# Revit family: Building-ConnessioniIEC309-GEWISS-44IB-PRESE-INTERBLOCCATE_IP44_SENZA_FONDO_FUS
name_source: partatom
category: Apparecchi elettrici
units: mm (PartAtom-declared; Revit-internal decimal feet)

## family parameters
Condiviso = No
Host = Superficie
Mantenere orientamento annotazione = Sì
Punto di calcolo locali = Sì
Quota connettore circolare = Usa diametro
Taglio con vuoti quando caricato = No
Tipo di parte = Normale

## types (22) — shared parameters
BLOCCO = B=C
Catalogo = BUILDING
Catalogo Serie = 44 IB
Codice Electrocod = 2220
Con fondo = No
FORMULA = 1000 mm  [stored 3.28084 ft]
Frequenza = 50/60 Hz
Frequenza nominale (Hz) = 50/60 Hz
Glow Wire Test = 850 °C (Parti attive) - 650 °C (Parti passive)
Glow wire test: = 850 °C (Parti attive) - 650 °C (Parti passive)
Grado di protezione = IP44
IDF = 20820749-807f-45a7-b37a-7863cab2ae49
IDT = d594ee1e-5beb-4100-9b20-8b248744bc80
Immagine tipo = IP44Fus.jpg
L = 155 mm  [stored 0.50853 ft]
N.poli = 1
POMELLO = bianco
PRESA = Giallo
Potere di interruzione fusibili = > 50 kA
Produttore = GEWISS S.p.A.
Prospetto di default = 1219 mm
Protezione = Base portafusibile (CBF)
Resistenza agli urti = IK08
SEO = Presa
STRUTTURA = RAL - 7035
STRUTTURA ALTA = blue
Scheda Tecnica = https://www.gewiss.com
Spostamento_S = 1000 mm  [stored 3.28084 ft]
Temperatura di funzionamento = -25 ÷ +40 °C
Temperatura di utilizzo = -25 +40 °C
Termopressione con biglia = 125 °C
Tipologia = Orizzontale
URL = https://www.gewiss.com
VETRO = Vetro
Versione file RFA = 21.4
Voltaggio = 0 V
W = 115 mm  [stored 0.377297 ft]

## per-type parameters (varying)
| type | Base portafusibile | Codice EAN | Colore | Colore: | Corrente nominale (A) | Corrente nominale (In) | Descrizione | Modello | N. poli | Numero di poli | Riferimento h | Tensione nominale |
| GW66130 - PRESA BL.OR.S.F.3P+T 16A 400V 6H CBF | E14 | 8011564029361 | Rosso | Rosso | 16 | 16 | PRESA BL.OR.S.F.3P+T 16A 400V 6H CBF | GW66130 | 3P+T | 3P+T | 6 | 380-415V |
| GW66131 - PRESA BL.OR.S.F.3P+N+T 16A 400V 6H CBF | E14 | 8011564029378 | Rosso | Rosso | 16 | 16 | PRESA BL.OR.S.F.3P+N+T 16A 400V 6H CBF | GW66131 | 3P+N+T | 3P+N+T | 6 | 380-415V |
| GW66137 - PRESA BL.OR.S.F.2P+T 32A 230V 6H CBF | E18 | 8011564029439 | Blu | Blu | 32 | 32 | PRESA BL.OR.S.F.2P+T 32A 230V 6H CBF | GW66137 | 2P+T | 2P+T | 6 | 200-250V |
| GW66125 - PRESA BL.OR.S.F.3P+N+T 16A 110V 4H CBF | E14 | 8011564029316 | Giallo | Giallo | 16 | 16 | PRESA BL.OR.S.F.3P+N+T 16A 110V 4H CBF | GW66125 | 3P+N+T | 3P+N+T | 4 | 100-130V |
| GW66136 - PRESA BL.OR.S.F.3P+N+T 32A 110V 4H CBF | E18 | 8011564029422 | Giallo | Giallo | 32 | 32 | PRESA BL.OR.S.F.3P+N+T 32A 110V 4H CBF | GW66136 | 3P+N+T | 3P+N+T | 4 | 100-130V |
| GW66132 - PRESA BL.OR.S.F.3P+T 16A 500V 7H CBF | gG | 8011564029385 | Nero | Nero | 16 | 16 | PRESA BL.OR.S.F.3P+T 16A 500V 7H CBF | GW66132 | 3P+T | 3P+T | 7 | 480-500V |
| GW66124 - PRESA BL.OR.S.F.3P+T 16A 110V 4H CBF | E14 | 8011564029309 | Giallo | Giallo | 16 | 16 | PRESA BL.OR.S.F.3P+T 16A 110V 4H CBF | GW66124 | 3P+T | 3P+T | 4 | 100-130V |
| GW66138 - PRESA BL.OR.S.F.3P+T 32A 230V 9H CBF | E18 | 8011564029446 | Blu | Blu | 32 | 32 | PRESA BL.OR.S.F.3P+T 32A 230V 9H CBF | GW66138 | 3P+T | 3P+T | 9 | 200-250V |
| GW66129 - PRESA BL.OR.S.F.2P+T 16A 400V 9H CBF | E14 | 8011564029354 | Rosso | Rosso | 16 | 16 | PRESA BL.OR.S.F.2P+T 16A 400V 9H CBF | GW66129 | 2P+T | 2P+T | 9 | 380-415V |
| GW66140 - PRESA BL.OR.S.F.2P+T 32A 400V 9H CBF | E18 | 8011564029460 | Rosso | Rosso | 32 | 32 | PRESA BL.OR.S.F.2P+T 32A 400V 9H CBF | GW66140 | 2P+T | 2P+T | 9 | 380-415V |
| GW66141 - PRESA BL.OR.S.F.3P+T 32A 400V 6H CBF | E18 | 8011564029477 | Rosso | Rosso | 32 | 32 | PRESA BL.OR.S.F.3P+T 32A 400V 6H CBF | GW66141 | 3P+T | 3P+T | 6 | 380-415V |
| GW66142 - PRESA BL.OR.S.F.3P+N+T 32A 400V 6H CBF | E18 | 8011564029484 | Rosso | Rosso | 32 | 32 | PRESA BL.OR.S.F.3P+N+T 32A 400V 6H CBF | GW66142 | 3P+N+T | 3P+N+T | 6 | 380-415V |
| GW66133 - PRESA BL.OR.S.F.3P+N+T 16A 500V 7H CBF | gG | 8011564029392 | Nero | Nero | 16 | 16 | PRESA BL.OR.S.F.3P+N+T 16A 500V 7H CBF | GW66133 | 3P+N+T | 3P+N+T | 7 | 480-500V |
| GW66134 - PRESA BL.OR.S.F.2P+T 32A 110V 4H CBF | E18 | 8011564029408 | Giallo | Giallo | 32 | 32 | PRESA BL.OR.S.F.2P+T 32A 110V 4H CBF | GW66134 | 2P+T | 2P+T | 4 | 100-130V |
| GW66135 - PRESA BL.OR.S.F.3P+T 32A 110V 4H CBF | E18 | 8011564029415 | Giallo | Giallo | 32 | 32 | PRESA BL.OR.S.F.3P+T 32A 110V 4H CBF | GW66135 | 3P+T | 3P+T | 4 | 100-130V |
| GW66128 - PRESA BL.OR.S.F.3P+N+T 16A 230V 9H CBF | E14 | 8011564029347 | Blu | Blu | 16 | 16 | PRESA BL.OR.S.F.3P+N+T 16A 230V 9H CBF | GW66128 | 3P+N+T | 3P+N+T | 9 | 200-250V |
| GW66143 - PRESA BL.OR.S.F.3P+T 32A 500V 7H CBF | gG | 8011564029491 | Nero | Nero | 32 | 32 | PRESA BL.OR.S.F.3P+T 32A 500V 7H CBF | GW66143 | 3P+T | 3P+T | 7 | 480-500V |
| GW66123 - PRESA BL.OR.S.F.2P+T 16A 110V 4H CBF | E14 | 8011564029293 | Giallo | Giallo | 16 | 16 | PRESA BL.OR.S.F.2P+T 16A 110V 4H CBF | GW66123 | 2P+T | 2P+T | 4 | 100-130V |
| GW66127 - PRESA BL.OR.S.F.3P+T 16A 230V 9H CBF | E14 | 8011564029330 | Blu | Blu | 16 | 16 | PRESA BL.OR.S.F.3P+T 16A 230V 9H CBF | GW66127 | 3P+T | 3P+T | 9 | 200-250V |
| GW66139 - PRESA BL.OR.S.F.3P+N+T 32A 230V 9H CBF | E18 | 8011564029453 | Blu | Blu | 32 | 32 | PRESA BL.OR.S.F.3P+N+T 32A 230V 9H CBF | GW66139 | 3P+N+T | 3P+N+T | 9 | 200-250V |
| GW66144 - PRESA BL.OR.S.F.3P+N+T 32A 500V 7H CBF | gG | 8011564029507 | Nero | Nero | 32 | 32 | PRESA BL.OR.S.F.3P+N+T 32A 500V 7H CBF | GW66144 | 3P+N+T | 3P+N+T | 7 | 480-500V |
| GW66126 - PRESA BL.OR.S.F.2P+T 16A 230V 6H CBF | E14 | 8011564029323 | Blu | Blu | 16 | 16 | PRESA BL.OR.S.F.2P+T 16A 230V 6H CBF | GW66126 | 2P+T | 2P+T | 6 | 200-250V |

note: [stored X ft] marks values corroborated as IEEE doubles in the binary element streams (Revit-internal decimal feet)

## geometry (parser evidence)
native form markers: Sweep x4
no freeform markers — native parametric forms only
